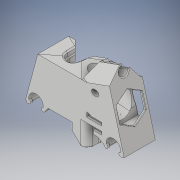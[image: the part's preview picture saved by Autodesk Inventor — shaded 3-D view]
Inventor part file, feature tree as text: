
AUTODESK INVENTOR PART (.ipt)
format: ipt  version: 2017 (Build 210142000, 142)  size: 1,959,936 bytes
history: native  units: in
note: dims shown in document units (in); Inventor stores cm internally (conversion verified against a paired STEP export)
features: other x1, fillet x1
ambient origin geometry x8: Origin, YZ Plane, XZ Plane, XY Plane, X Axis, Y Axis, Z Axis, Center Point
bodies: Solid1 (feature_tree)
feature tree (2):
  other  "14_tete.STEP"
  fillet  "Congé88"  [1 undecoded]
note: 1 required parameter value undecoded (feature->parameter linkage not recoverable at this tier; creation-order binding heuristic only, values carry confidence <= 0.55)
